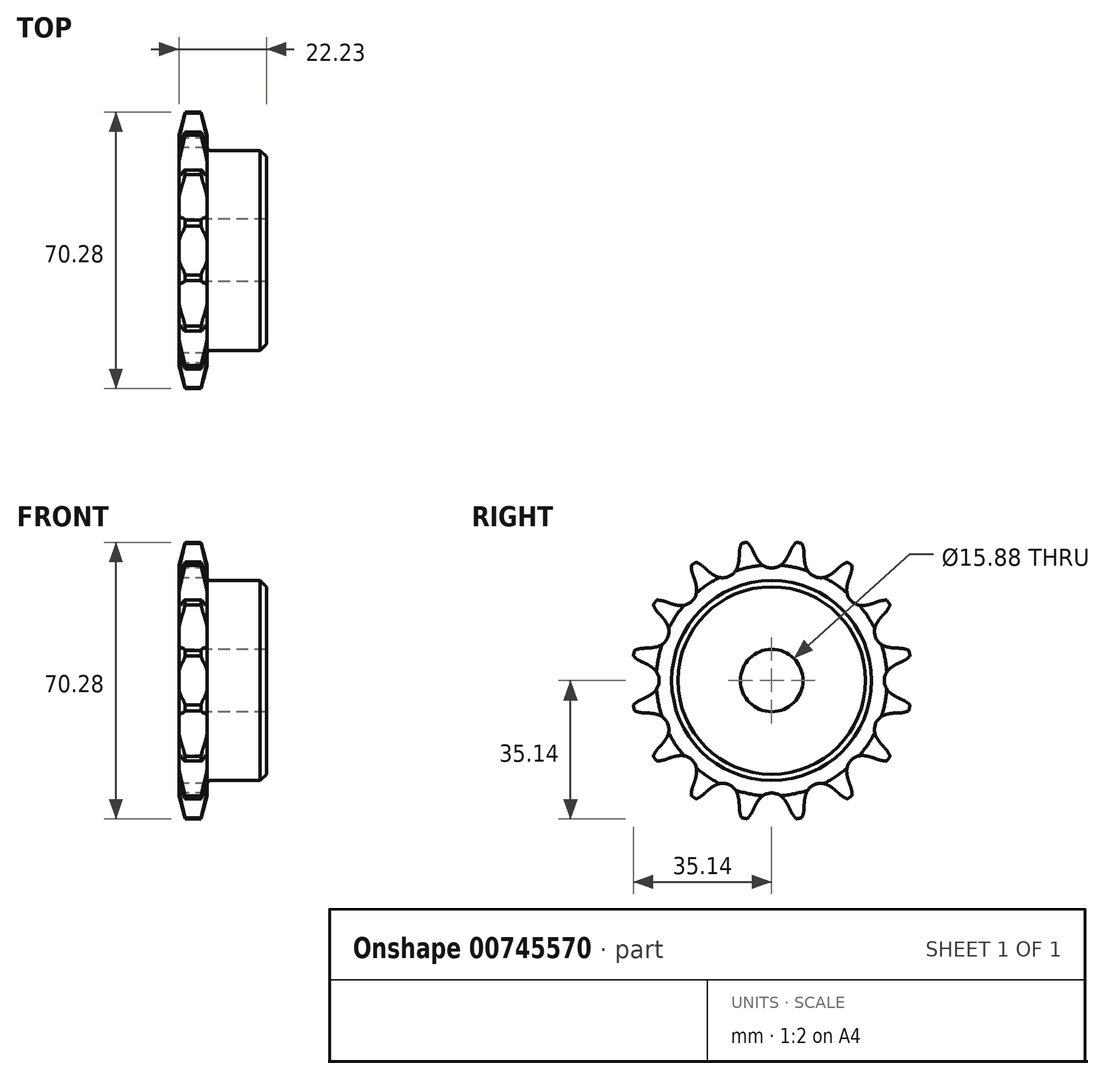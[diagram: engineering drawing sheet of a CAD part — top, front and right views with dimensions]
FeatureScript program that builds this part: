
annotation { "Feature Type Name" : "Feature", "Feature Type Description" : "" }
export const myFeature = defineFeature(function(context is Context, id is Id, definition is map)
    precondition{}
    {
        {
            var Q0;
            Q0=qCreatedBy(makeId("Front.planeOp"),FACE);
            var sketch = newSketch(context, id + "F0", { "sketchPlane" : qUnion([Q0])});
            skLineSegment(sketch, "E0", {"start": v(0, 0) * mm, "end": v(66.48, 0) * mm, "construction": true});
            skLineSegment(sketch, "E1.bottom", {"start": v(0, 7.94) * mm, "end": v(22.23, 7.94) * mm});
            skLineSegment(sketch, "E1.top", {"start": v(0, 25.4) * mm, "end": v(22.23, 25.4) * mm});
            skLineSegment(sketch, "E1.left", {"start": v(0, 7.94) * mm, "end": v(0, 25.4) * mm});
            skLineSegment(sketch, "E1.right", {"start": v(22.23, 7.94) * mm, "end": v(22.23, 25.4) * mm});
            skLineSegment(sketch, "E2.bottom", {"start": v(0, 7.94) * mm, "end": v(7.21, 7.94) * mm});
            skLineSegment(sketch, "E2.top", {"start": v(0, 35.69) * mm, "end": v(7.21, 35.69) * mm});
            skLineSegment(sketch, "E2.left", {"start": v(0, 7.94) * mm, "end": v(0, 35.69) * mm});
            skLineSegment(sketch, "E2.right", {"start": v(7.21, 7.94) * mm, "end": v(7.21, 35.69) * mm});
            skSolve(sketch);
        }
        {
            var Q0;
            {var subQ5=sQuery(id+"F0.wireOp",EDGE,"E2.bottom");Q0=makeQuery(id+"F0.imprint","IMPRINT",FACE,{"disambiguationData":[TD([[makeQuery(id+"F0.imprint","IMPRINT",EDGE,{"derivedFrom":subQ5}),1.0]])]});}
            var Q1;
            {var subQ0=sQuery(id+"F0.wireOp",EDGE,"E1.bottom");Q1=makeQuery(id+"F0.imprint","IMPRINT",FACE,{"disambiguationData":[TD([[makeQuery(id+"F0.imprint","IMPRINT",EDGE,{"derivedFrom":subQ0}),1.0]])]});}
            var Q2;
            {var subQ5=sQuery(id+"F0.wireOp",EDGE,"E2.top");Q2=makeQuery(id+"F0.imprint","IMPRINT",FACE,{"disambiguationData":[TD([[makeQuery(id+"F0.imprint","IMPRINT",EDGE,{"derivedFrom":subQ5}),-1.0]])]});}
            var Q3;
            Q3=sQuery(id+"F0.wireOp",EDGE,"E0");
            revolve(context, id + "F1", {"surfaceOperationType" : NewSurfaceOperationType.NEW, "entities" : qUnion([Q0, Q1, Q2]), "axis" : qUnion([Q3]), "revolveType" : RevolveType.FULL});
        }
        {
            var Q0;
            Q0=makeQuery(id+"F1.opRevolve","SWEPT_EDGE",EDGE,{"disambiguationData":[OSD([sQuery(id+"F0.wireOp",EDGE,"E2.top"),sQuery(id+"F0.wireOp",EDGE,"E2.left")])]});
            var Q1;
            Q1=makeQuery(id+"F1.opRevolve","SWEPT_EDGE",EDGE,{"disambiguationData":[OSD([sQuery(id+"F0.wireOp",EDGE,"E2.top"),sQuery(id+"F0.wireOp",EDGE,"E2.right")])]});
            chamfer(context, id + "F2", {"entities" : qUnion([Q0, Q1]), "chamferType" : ChamferType.TWO_OFFSETS, "width1" : 6.35 * mm, "oppositeDirection" : false, "width2" : 1.59 * mm, "tangentPropagation" : true});
        }
        {
            var Q0;
            Q0=makeQuery(id+"F1.opRevolve","SWEPT_EDGE",EDGE,{"disambiguationData":[OSD([sQuery(id+"F0.wireOp",EDGE,"E1.top"),sQuery(id+"F0.wireOp",EDGE,"E1.right")])]});
            chamfer(context, id + "F3", {"entities" : qUnion([Q0]), "width" : 1.59 * mm, "tangentPropagation" : true});
        }
        {
            var Q0;
            Q0=makeQuery(id+"F1.opRevolve","SWEPT_EDGE",EDGE,{"disambiguationData":[OSD([sQuery(id+"F0.wireOp",EDGE,"E1.top"),sQuery(id+"F0.wireOp",EDGE,"E2.right")])]});
            fillet(context, id + "F4", {"entities" : qUnion([Q0]), "tangentPropagation" : true, "radius" : 0.8 * mm, "defaultsChanged" : false, "vertexSettings" : [], "allowEdgeOverflow" : false});
        }
        {
            var Q0;
            Q0=qCreatedBy(makeId("Right.planeOp"),FACE);
            var sketch = newSketch(context, id + "F5", { "sketchPlane" : qUnion([Q0])});
            skCircle(sketch, "E3", {"center": v(0, 0) * mm, "radius": 32.55 * mm, "construction": true});
            skLineSegment(sketch, "E4", {"start": v(0, 0) * mm, "end": v(0, 32.55) * mm, "construction": true});
            skLineSegment(sketch, "E5", {"start": v(0, 32.55) * mm, "end": v(-32.2, 32.55) * mm, "construction": true});
            skLineSegment(sketch, "E6", {"start": v(0, 32.55) * mm, "end": v(-5, 36.56) * mm, "construction": true});
            skLineSegment(sketch, "E7", {"start": v(-5, 36.56) * mm, "end": v(4.46, 32.3) * mm, "construction": true});
            skLineSegment(sketch, "E8", {"start": v(4.46, 32.3) * mm, "end": v(4.82, 33.1) * mm});
            skLineSegment(sketch, "E9", {"start": v(4.82, 33.1) * mm, "end": v(10.16, 44.96) * mm, "construction": true});
            skLineSegment(sketch, "E10", {"start": v(0, 0) * mm, "end": v(7.13, 35.85) * mm, "construction": true});
            skArc(sketch, "E11", {"start": v(7.13, 35.85) * mm, "mid": v(5.78, 34.63) * mm, "end": v(4.82, 33.1) * mm});
            skArc(sketch, "E12", {"start": v(4.82, 33.1) * mm, "mid": v(15.87, 26.15) * mm, "end": v(7.13, 35.85) * mm, "construction": true});
            skArc(sketch, "E13", {"start": v(4.46, 32.3) * mm, "mid": v(-13.83, 41.97) * mm, "end": v(3.1, 30.07) * mm, "construction": true});
            skArc(sketch, "E14", {"start": v(3.1, 30.07) * mm, "mid": v(3.84, 31.14) * mm, "end": v(4.46, 32.3) * mm});
            skArc(sketch, "E15.MirrorCS", {"start": v(-7.13, 35.85) * mm, "mid": v(-5.78, 34.63) * mm, "end": v(-4.82, 33.1) * mm});
            skArc(sketch, "E16.MirrorCS", {"start": v(-3.1, 30.07) * mm, "mid": v(-3.84, 31.14) * mm, "end": v(-4.46, 32.3) * mm});
            skLineSegment(sketch, "E17.MirrorCS", {"start": v(-4.46, 32.3) * mm, "end": v(-4.82, 33.1) * mm});
            skArc(sketch, "E18", {"start": v(-3.1, 30.07) * mm, "mid": v(0, 28.59) * mm, "end": v(3.1, 30.07) * mm});
            skArc(sketch, "E19", {"start": v(3.1, 30.07) * mm, "mid": v(0, 36.51) * mm, "end": v(-3.1, 30.07) * mm, "construction": true});
            skArc(sketch, "E20.1.0", {"start": v(-14.36, 26.6) * mm, "mid": v(-10.94, 26.41) * mm, "end": v(-8.65, 28.96) * mm});
            skLineSegment(sketch, "E20.1.1", {"start": v(-16.48, 28.14) * mm, "end": v(-17.12, 28.74) * mm});
            skArc(sketch, "E20.1.2", {"start": v(-20.3, 30.4) * mm, "mid": v(-18.6, 29.79) * mm, "end": v(-17.12, 28.74) * mm});
            skArc(sketch, "E20.1.3", {"start": v(-7.13, 35.85) * mm, "mid": v(-7.91, 34.21) * mm, "end": v(-8.22, 32.42) * mm});
            skArc(sketch, "E20.1.4", {"start": v(-14.36, 26.6) * mm, "mid": v(-15.47, 27.3) * mm, "end": v(-16.48, 28.14) * mm});
            skLineSegment(sketch, "E20.1.5", {"start": v(-8.24, 31.55) * mm, "end": v(-8.22, 32.42) * mm});
            skArc(sketch, "E20.1.6", {"start": v(-8.65, 28.96) * mm, "mid": v(-8.37, 30.24) * mm, "end": v(-8.24, 31.55) * mm});
            skArc(sketch, "E20.2.0", {"start": v(-23.45, 19.08) * mm, "mid": v(-20.21, 20.21) * mm, "end": v(-19.08, 23.45) * mm});
            skLineSegment(sketch, "E20.2.1", {"start": v(-26, 19.69) * mm, "end": v(-26.8, 20) * mm});
            skArc(sketch, "E20.2.2", {"start": v(-30.4, 20.3) * mm, "mid": v(-28.58, 20.4) * mm, "end": v(-26.8, 20) * mm});
            skArc(sketch, "E20.2.3", {"start": v(-20.3, 30.4) * mm, "mid": v(-20.4, 28.58) * mm, "end": v(-20, 26.8) * mm});
            skArc(sketch, "E20.2.4", {"start": v(-23.45, 19.08) * mm, "mid": v(-24.74, 19.3) * mm, "end": v(-26, 19.69) * mm});
            skLineSegment(sketch, "E20.2.5", {"start": v(-19.69, 26) * mm, "end": v(-20, 26.8) * mm});
            skArc(sketch, "E20.2.6", {"start": v(-19.08, 23.45) * mm, "mid": v(-19.3, 24.74) * mm, "end": v(-19.69, 26) * mm});
            skArc(sketch, "E20.3.0", {"start": v(-28.96, 8.65) * mm, "mid": v(-26.41, 10.94) * mm, "end": v(-26.6, 14.36) * mm});
            skLineSegment(sketch, "E20.3.1", {"start": v(-31.55, 8.24) * mm, "end": v(-32.42, 8.22) * mm});
            skArc(sketch, "E20.3.2", {"start": v(-35.85, 7.13) * mm, "mid": v(-34.21, 7.91) * mm, "end": v(-32.42, 8.22) * mm});
            skArc(sketch, "E20.3.3", {"start": v(-30.4, 20.3) * mm, "mid": v(-29.79, 18.6) * mm, "end": v(-28.74, 17.12) * mm});
            skArc(sketch, "E20.3.4", {"start": v(-28.96, 8.65) * mm, "mid": v(-30.24, 8.37) * mm, "end": v(-31.55, 8.24) * mm});
            skLineSegment(sketch, "E20.3.5", {"start": v(-28.14, 16.48) * mm, "end": v(-28.74, 17.12) * mm});
            skArc(sketch, "E20.3.6", {"start": v(-26.6, 14.36) * mm, "mid": v(-27.3, 15.47) * mm, "end": v(-28.14, 16.48) * mm});
            skArc(sketch, "E20.4.0", {"start": v(-30.07, -3.1) * mm, "mid": v(-28.59, 0) * mm, "end": v(-30.07, 3.1) * mm});
            skLineSegment(sketch, "E20.4.1", {"start": v(-32.3, -4.46) * mm, "end": v(-33.1, -4.82) * mm});
            skArc(sketch, "E20.4.2", {"start": v(-35.85, -7.13) * mm, "mid": v(-34.63, -5.78) * mm, "end": v(-33.1, -4.82) * mm});
            skArc(sketch, "E20.4.3", {"start": v(-35.85, 7.13) * mm, "mid": v(-34.63, 5.78) * mm, "end": v(-33.1, 4.82) * mm});
            skArc(sketch, "E20.4.4", {"start": v(-30.07, -3.1) * mm, "mid": v(-31.14, -3.84) * mm, "end": v(-32.3, -4.46) * mm});
            skLineSegment(sketch, "E20.4.5", {"start": v(-32.3, 4.46) * mm, "end": v(-33.1, 4.82) * mm});
            skArc(sketch, "E20.4.6", {"start": v(-30.07, 3.1) * mm, "mid": v(-31.14, 3.84) * mm, "end": v(-32.3, 4.46) * mm});
            skArc(sketch, "E20.5.0", {"start": v(-26.6, -14.36) * mm, "mid": v(-26.41, -10.94) * mm, "end": v(-28.96, -8.65) * mm});
            skLineSegment(sketch, "E20.5.1", {"start": v(-28.14, -16.48) * mm, "end": v(-28.74, -17.12) * mm});
            skArc(sketch, "E20.5.2", {"start": v(-30.4, -20.3) * mm, "mid": v(-29.79, -18.6) * mm, "end": v(-28.74, -17.12) * mm});
            skArc(sketch, "E20.5.3", {"start": v(-35.85, -7.13) * mm, "mid": v(-34.21, -7.91) * mm, "end": v(-32.42, -8.22) * mm});
            skArc(sketch, "E20.5.4", {"start": v(-26.6, -14.36) * mm, "mid": v(-27.3, -15.47) * mm, "end": v(-28.14, -16.48) * mm});
            skLineSegment(sketch, "E20.5.5", {"start": v(-31.55, -8.24) * mm, "end": v(-32.42, -8.22) * mm});
            skArc(sketch, "E20.5.6", {"start": v(-28.96, -8.65) * mm, "mid": v(-30.24, -8.37) * mm, "end": v(-31.55, -8.24) * mm});
            skArc(sketch, "E20.6.0", {"start": v(-19.08, -23.45) * mm, "mid": v(-20.21, -20.21) * mm, "end": v(-23.45, -19.08) * mm});
            skLineSegment(sketch, "E20.6.1", {"start": v(-19.69, -26) * mm, "end": v(-20, -26.8) * mm});
            skArc(sketch, "E20.6.2", {"start": v(-20.3, -30.4) * mm, "mid": v(-20.4, -28.58) * mm, "end": v(-20, -26.8) * mm});
            skArc(sketch, "E20.6.3", {"start": v(-30.4, -20.3) * mm, "mid": v(-28.58, -20.4) * mm, "end": v(-26.8, -20) * mm});
            skArc(sketch, "E20.6.4", {"start": v(-19.08, -23.45) * mm, "mid": v(-19.3, -24.74) * mm, "end": v(-19.69, -26) * mm});
            skLineSegment(sketch, "E20.6.5", {"start": v(-26, -19.69) * mm, "end": v(-26.8, -20) * mm});
            skArc(sketch, "E20.6.6", {"start": v(-23.45, -19.08) * mm, "mid": v(-24.74, -19.3) * mm, "end": v(-26, -19.69) * mm});
            skArc(sketch, "E20.7.0", {"start": v(-8.65, -28.96) * mm, "mid": v(-10.94, -26.41) * mm, "end": v(-14.36, -26.6) * mm});
            skLineSegment(sketch, "E20.7.1", {"start": v(-8.24, -31.55) * mm, "end": v(-8.22, -32.42) * mm});
            skArc(sketch, "E20.7.2", {"start": v(-7.13, -35.85) * mm, "mid": v(-7.91, -34.21) * mm, "end": v(-8.22, -32.42) * mm});
            skArc(sketch, "E20.7.3", {"start": v(-20.3, -30.4) * mm, "mid": v(-18.6, -29.79) * mm, "end": v(-17.12, -28.74) * mm});
            skArc(sketch, "E20.7.4", {"start": v(-8.65, -28.96) * mm, "mid": v(-8.37, -30.24) * mm, "end": v(-8.24, -31.55) * mm});
            skLineSegment(sketch, "E20.7.5", {"start": v(-16.48, -28.14) * mm, "end": v(-17.12, -28.74) * mm});
            skArc(sketch, "E20.7.6", {"start": v(-14.36, -26.6) * mm, "mid": v(-15.47, -27.3) * mm, "end": v(-16.48, -28.14) * mm});
            skArc(sketch, "E20.8.0", {"start": v(3.1, -30.07) * mm, "mid": v(0, -28.59) * mm, "end": v(-3.1, -30.07) * mm});
            skLineSegment(sketch, "E20.8.1", {"start": v(4.46, -32.3) * mm, "end": v(4.82, -33.1) * mm});
            skArc(sketch, "E20.8.2", {"start": v(7.13, -35.85) * mm, "mid": v(5.78, -34.63) * mm, "end": v(4.82, -33.1) * mm});
            skArc(sketch, "E20.8.3", {"start": v(-7.13, -35.85) * mm, "mid": v(-5.78, -34.63) * mm, "end": v(-4.82, -33.1) * mm});
            skArc(sketch, "E20.8.4", {"start": v(3.1, -30.07) * mm, "mid": v(3.84, -31.14) * mm, "end": v(4.46, -32.3) * mm});
            skLineSegment(sketch, "E20.8.5", {"start": v(-4.46, -32.3) * mm, "end": v(-4.82, -33.1) * mm});
            skArc(sketch, "E20.8.6", {"start": v(-3.1, -30.07) * mm, "mid": v(-3.84, -31.14) * mm, "end": v(-4.46, -32.3) * mm});
            skArc(sketch, "E20.9.0", {"start": v(14.36, -26.6) * mm, "mid": v(10.94, -26.41) * mm, "end": v(8.65, -28.96) * mm});
            skLineSegment(sketch, "E20.9.1", {"start": v(16.48, -28.14) * mm, "end": v(17.12, -28.74) * mm});
            skArc(sketch, "E20.9.2", {"start": v(20.3, -30.4) * mm, "mid": v(18.6, -29.79) * mm, "end": v(17.12, -28.74) * mm});
            skArc(sketch, "E20.9.3", {"start": v(7.13, -35.85) * mm, "mid": v(7.91, -34.21) * mm, "end": v(8.22, -32.42) * mm});
            skArc(sketch, "E20.9.4", {"start": v(14.36, -26.6) * mm, "mid": v(15.47, -27.3) * mm, "end": v(16.48, -28.14) * mm});
            skLineSegment(sketch, "E20.9.5", {"start": v(8.24, -31.55) * mm, "end": v(8.22, -32.42) * mm});
            skArc(sketch, "E20.9.6", {"start": v(8.65, -28.96) * mm, "mid": v(8.37, -30.24) * mm, "end": v(8.24, -31.55) * mm});
            skArc(sketch, "E20.10.0", {"start": v(23.45, -19.08) * mm, "mid": v(20.21, -20.21) * mm, "end": v(19.08, -23.45) * mm});
            skLineSegment(sketch, "E20.10.1", {"start": v(26, -19.69) * mm, "end": v(26.8, -20) * mm});
            skArc(sketch, "E20.10.2", {"start": v(30.4, -20.3) * mm, "mid": v(28.58, -20.4) * mm, "end": v(26.8, -20) * mm});
            skArc(sketch, "E20.10.3", {"start": v(20.3, -30.4) * mm, "mid": v(20.4, -28.58) * mm, "end": v(20, -26.8) * mm});
            skArc(sketch, "E20.10.4", {"start": v(23.45, -19.08) * mm, "mid": v(24.74, -19.3) * mm, "end": v(26, -19.69) * mm});
            skLineSegment(sketch, "E20.10.5", {"start": v(19.69, -26) * mm, "end": v(20, -26.8) * mm});
            skArc(sketch, "E20.10.6", {"start": v(19.08, -23.45) * mm, "mid": v(19.3, -24.74) * mm, "end": v(19.69, -26) * mm});
            skArc(sketch, "E20.11.0", {"start": v(28.96, -8.65) * mm, "mid": v(26.41, -10.94) * mm, "end": v(26.6, -14.36) * mm});
            skLineSegment(sketch, "E20.11.1", {"start": v(31.55, -8.24) * mm, "end": v(32.42, -8.22) * mm});
            skArc(sketch, "E20.11.2", {"start": v(35.85, -7.13) * mm, "mid": v(34.21, -7.91) * mm, "end": v(32.42, -8.22) * mm});
            skArc(sketch, "E20.11.3", {"start": v(30.4, -20.3) * mm, "mid": v(29.79, -18.6) * mm, "end": v(28.74, -17.12) * mm});
            skArc(sketch, "E20.11.4", {"start": v(28.96, -8.65) * mm, "mid": v(30.24, -8.37) * mm, "end": v(31.55, -8.24) * mm});
            skLineSegment(sketch, "E20.11.5", {"start": v(28.14, -16.48) * mm, "end": v(28.74, -17.12) * mm});
            skArc(sketch, "E20.11.6", {"start": v(26.6, -14.36) * mm, "mid": v(27.3, -15.47) * mm, "end": v(28.14, -16.48) * mm});
            skArc(sketch, "E20.12.0", {"start": v(30.07, 3.1) * mm, "mid": v(28.59, 0) * mm, "end": v(30.07, -3.1) * mm});
            skLineSegment(sketch, "E20.12.1", {"start": v(32.3, 4.46) * mm, "end": v(33.1, 4.82) * mm});
            skArc(sketch, "E20.12.2", {"start": v(35.85, 7.13) * mm, "mid": v(34.63, 5.78) * mm, "end": v(33.1, 4.82) * mm});
            skArc(sketch, "E20.12.3", {"start": v(35.85, -7.13) * mm, "mid": v(34.63, -5.78) * mm, "end": v(33.1, -4.82) * mm});
            skArc(sketch, "E20.12.4", {"start": v(30.07, 3.1) * mm, "mid": v(31.14, 3.84) * mm, "end": v(32.3, 4.46) * mm});
            skLineSegment(sketch, "E20.12.5", {"start": v(32.3, -4.46) * mm, "end": v(33.1, -4.82) * mm});
            skArc(sketch, "E20.12.6", {"start": v(30.07, -3.1) * mm, "mid": v(31.14, -3.84) * mm, "end": v(32.3, -4.46) * mm});
            skArc(sketch, "E20.13.0", {"start": v(26.6, 14.36) * mm, "mid": v(26.41, 10.94) * mm, "end": v(28.96, 8.65) * mm});
            skLineSegment(sketch, "E20.13.1", {"start": v(28.14, 16.48) * mm, "end": v(28.74, 17.12) * mm});
            skArc(sketch, "E20.13.2", {"start": v(30.4, 20.3) * mm, "mid": v(29.79, 18.6) * mm, "end": v(28.74, 17.12) * mm});
            skArc(sketch, "E20.13.3", {"start": v(35.85, 7.13) * mm, "mid": v(34.21, 7.91) * mm, "end": v(32.42, 8.22) * mm});
            skArc(sketch, "E20.13.4", {"start": v(26.6, 14.36) * mm, "mid": v(27.3, 15.47) * mm, "end": v(28.14, 16.48) * mm});
            skLineSegment(sketch, "E20.13.5", {"start": v(31.55, 8.24) * mm, "end": v(32.42, 8.22) * mm});
            skArc(sketch, "E20.13.6", {"start": v(28.96, 8.65) * mm, "mid": v(30.24, 8.37) * mm, "end": v(31.55, 8.24) * mm});
            skArc(sketch, "E20.14.0", {"start": v(19.08, 23.45) * mm, "mid": v(20.21, 20.21) * mm, "end": v(23.45, 19.08) * mm});
            skLineSegment(sketch, "E20.14.1", {"start": v(19.69, 26) * mm, "end": v(20, 26.8) * mm});
            skArc(sketch, "E20.14.2", {"start": v(20.3, 30.4) * mm, "mid": v(20.4, 28.58) * mm, "end": v(20, 26.8) * mm});
            skArc(sketch, "E20.14.3", {"start": v(30.4, 20.3) * mm, "mid": v(28.58, 20.4) * mm, "end": v(26.8, 20) * mm});
            skArc(sketch, "E20.14.4", {"start": v(19.08, 23.45) * mm, "mid": v(19.3, 24.74) * mm, "end": v(19.69, 26) * mm});
            skLineSegment(sketch, "E20.14.5", {"start": v(26, 19.69) * mm, "end": v(26.8, 20) * mm});
            skArc(sketch, "E20.14.6", {"start": v(23.45, 19.08) * mm, "mid": v(24.74, 19.3) * mm, "end": v(26, 19.69) * mm});
            skArc(sketch, "E20.15.0", {"start": v(8.65, 28.96) * mm, "mid": v(10.94, 26.41) * mm, "end": v(14.36, 26.6) * mm});
            skLineSegment(sketch, "E20.15.1", {"start": v(8.24, 31.55) * mm, "end": v(8.22, 32.42) * mm});
            skArc(sketch, "E20.15.2", {"start": v(7.13, 35.85) * mm, "mid": v(7.91, 34.21) * mm, "end": v(8.22, 32.42) * mm});
            skArc(sketch, "E20.15.3", {"start": v(20.3, 30.4) * mm, "mid": v(18.6, 29.79) * mm, "end": v(17.12, 28.74) * mm});
            skArc(sketch, "E20.15.4", {"start": v(8.65, 28.96) * mm, "mid": v(8.37, 30.24) * mm, "end": v(8.24, 31.55) * mm});
            skLineSegment(sketch, "E20.15.5", {"start": v(16.48, 28.14) * mm, "end": v(17.12, 28.74) * mm});
            skArc(sketch, "E20.15.6", {"start": v(14.36, 26.6) * mm, "mid": v(15.47, 27.3) * mm, "end": v(16.48, 28.14) * mm});
            skSolve(sketch);
        }
        {
            var Q0;
            Q0=makeQuery(id+"F5.imprint","IMPRINT",FACE,{"disambiguationData":[TD([[makeQuery(id+"F5.imprint","IMPRINT",EDGE,{"derivedFrom":sQuery(id+"F5.wireOp",EDGE,"E8")}),-1.0]])]});
            extrude(context, id + "F6", {"entities" : qUnion([Q0]), "operationType" : NewBodyOperationType.INTERSECT, "endBound" : BoundingType.UP_TO_NEXT, "depth" : 25.4 * mm, "offsetDistance" : 25.4 * mm});
        }
    });
